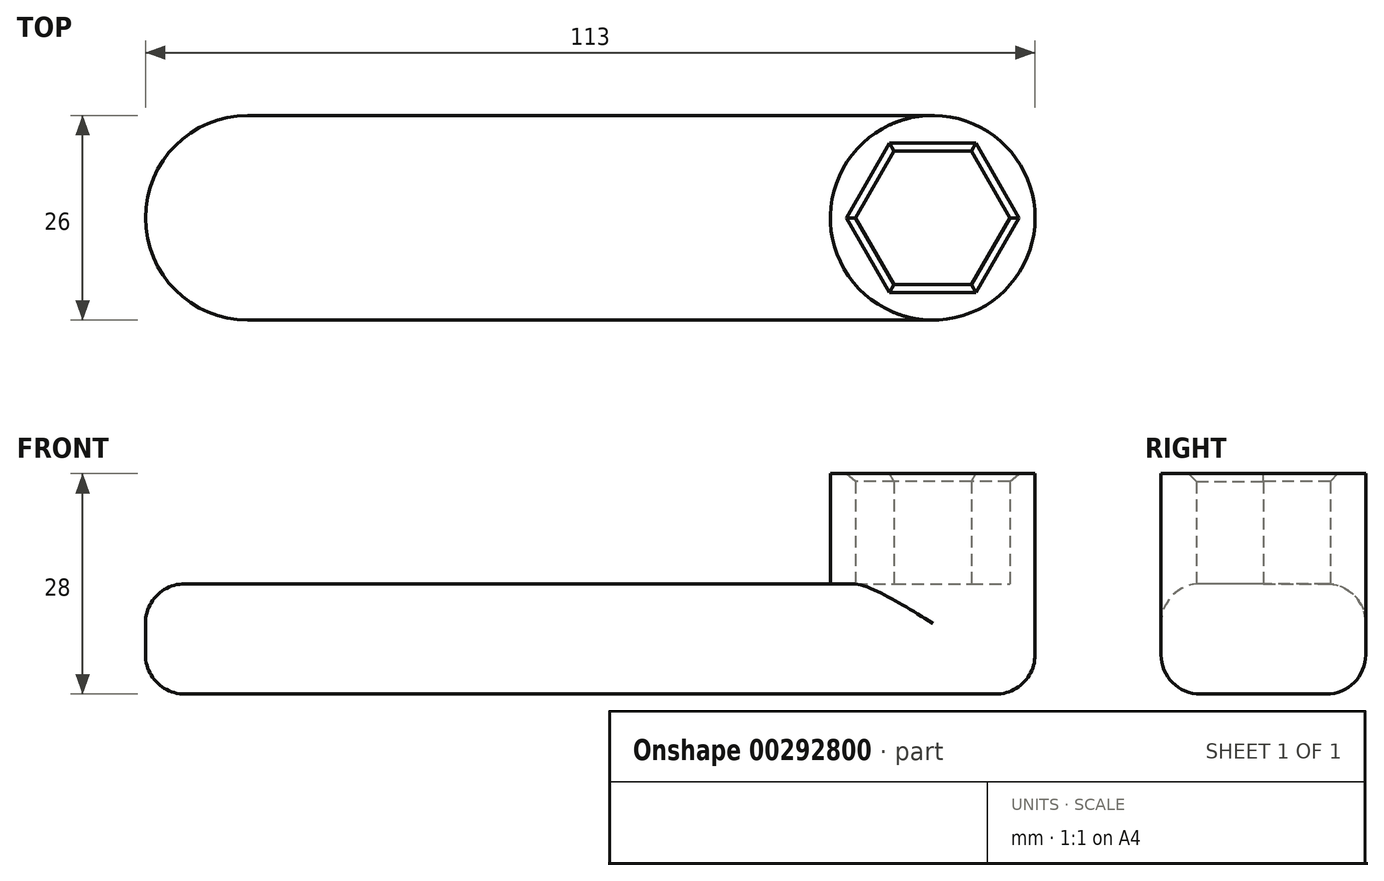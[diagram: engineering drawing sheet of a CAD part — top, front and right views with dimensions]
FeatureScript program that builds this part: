
annotation { "Feature Type Name" : "Feature", "Feature Type Description" : "" }
export const myFeature = defineFeature(function(context is Context, id is Id, definition is map)
    precondition{}
    {
        {
            var Q0;
            Q0=qCreatedBy(makeId("Top.planeOp"),FACE);
            var sketch = newSketch(context, id + "F0", { "sketchPlane" : qUnion([Q0])});
            skCircle(sketch, "E0.cCircle", {"center": v(0, 0) * mm, "radius": 8.5 * mm, "construction": true});
            skLineSegment(sketch, "E0.0", {"start": v(-4.9, 8.5) * mm, "end": v(4.9, 8.5) * mm});
            skLineSegment(sketch, "E0.1", {"start": v(4.9, 8.5) * mm, "end": v(9.81, 0) * mm});
            skLineSegment(sketch, "E0.2", {"start": v(9.81, 0) * mm, "end": v(4.9, -8.5) * mm});
            skLineSegment(sketch, "E0.3", {"start": v(4.9, -8.5) * mm, "end": v(-4.9, -8.5) * mm});
            skLineSegment(sketch, "E0.4", {"start": v(-4.9, -8.5) * mm, "end": v(-9.81, 0) * mm});
            skLineSegment(sketch, "E0.5", {"start": v(-9.81, 0) * mm, "end": v(-4.9, 8.5) * mm});
            skPoint(sketch, "E0.0.midPoint", {"position": v(0, 8.5) * mm});
            skCircle(sketch, "E1", {"center": v(0, 0) * mm, "radius": 13 * mm});
            skSolve(sketch);
        }
        {
            var Q0;
            Q0 = qSketchRegion(id + "F0", true);
            extrude(context, id + "F1", {"entities" : qUnion([Q0]), "depth" : 14 * mm});
        }
        {
            var Q0;
            Q0=makeQuery(id+"F1.opExtrude","CAP_FACE",FACE,{"disambiguationData":[OSD([sQuery(id+"F0.wireOp",EDGE,"E0.0"),sQuery(id+"F0.wireOp",EDGE,"E0.1"),sQuery(id+"F0.wireOp",EDGE,"E0.2"),sQuery(id+"F0.wireOp",EDGE,"E0.3"),sQuery(id+"F0.wireOp",EDGE,"E0.4"),sQuery(id+"F0.wireOp",EDGE,"E0.5"),sQuery(id+"F0.wireOp",EDGE,"E1")])],"isStart":true});
            var sketch = newSketch(context, id + "F2", { "sketchPlane" : qUnion([Q0])});
            skArc(sketch, "E2.0", {"start": v(0, -13) * mm, "mid": v(13, 0) * mm, "end": v(0, 13) * mm});
            skLineSegment(sketch, "E3", {"start": v(0, -13) * mm, "end": v(-100, -13) * mm});
            skLineSegment(sketch, "E4", {"start": v(0, 13) * mm, "end": v(-100, 13) * mm});
            skPoint(sketch, "E4.startSnap0", {"position": v(0, 8.5) * mm});
            skLineSegment(sketch, "E5", {"start": v(-100, 13) * mm, "end": v(-100, -13) * mm});
            skSolve(sketch);
        }
        {
            var Q0;
            Q0 = qSketchRegion(id + "F2", true);
            extrude(context, id + "F3", {"entities" : qUnion([Q0]), "operationType" : NewBodyOperationType.ADD, "depth" : 14 * mm});
        }
        {
            var Q0;
            Q0=makeQuery(id+"F1.opExtrude","CAP_EDGE",EDGE,{"disambiguationData":[OSD([sQuery(id+"F0.wireOp",EDGE,"E0.5")])],"isStart":false});
            var Q1;
            Q1=makeQuery(id+"F1.opExtrude","CAP_EDGE",EDGE,{"disambiguationData":[OSD([sQuery(id+"F0.wireOp",EDGE,"E0.0")])],"isStart":false});
            var Q2;
            Q2=makeQuery(id+"F1.opExtrude","CAP_EDGE",EDGE,{"disambiguationData":[OSD([sQuery(id+"F0.wireOp",EDGE,"E0.1")])],"isStart":false});
            var Q3;
            Q3=makeQuery(id+"F1.opExtrude","CAP_EDGE",EDGE,{"disambiguationData":[OSD([sQuery(id+"F0.wireOp",EDGE,"E0.2")])],"isStart":false});
            var Q4;
            Q4=makeQuery(id+"F1.opExtrude","CAP_EDGE",EDGE,{"disambiguationData":[OSD([sQuery(id+"F0.wireOp",EDGE,"E0.3")])],"isStart":false});
            var Q5;
            Q5=makeQuery(id+"F1.opExtrude","CAP_EDGE",EDGE,{"disambiguationData":[OSD([sQuery(id+"F0.wireOp",EDGE,"E0.4")])],"isStart":false});
            chamfer(context, id + "F4", {"entities" : qUnion([Q0, Q1, Q2, Q3, Q4, Q5]), "width" : 1 * mm, "tangentPropagation" : true});
        }
        {
            var Q0;
            Q0=makeQuery(id+"F3.opExtrude","SWEPT_EDGE",EDGE,{"disambiguationData":[OSD([sQuery(id+"F2.wireOp",EDGE,"E3"),sQuery(id+"F2.wireOp",EDGE,"E5")])]});
            var Q1;
            Q1=makeQuery(id+"F3.opExtrude","SWEPT_EDGE",EDGE,{"disambiguationData":[OSD([sQuery(id+"F2.wireOp",EDGE,"E4"),sQuery(id+"F2.wireOp",EDGE,"E5")])]});
            fillet(context, id + "F5", {"entities" : qUnion([Q0, Q1]), "radius" : 13 * mm, "tangentPropagation" : true, "allowEdgeOverflow" : false});
        }
        {
            var Q0;
            Q0=makeQuery(id+"F3.opExtrude","CAP_EDGE",EDGE,{"disambiguationData":[OSD([sQuery(id+"F2.wireOp",EDGE,"E3")])],"isStart":false});
            var Q1;
            Q1=makeQuery(id+"F3.opExtrude","CAP_EDGE",EDGE,{"disambiguationData":[OSD([sQuery(id+"F2.wireOp",EDGE,"E3")])],"isStart":true});
            fillet(context, id + "F6", {"entities" : qUnion([Q0, Q1]), "radius" : 5 * mm, "tangentPropagation" : true, "allowEdgeOverflow" : false});
        }
    });
